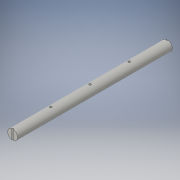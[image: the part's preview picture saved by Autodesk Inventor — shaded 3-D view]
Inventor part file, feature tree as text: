
AUTODESK INVENTOR PART (.ipt)
format: ipt  version: 2016 (Build 200138000, 138)  size: 138,752 bytes
history: native  units: in
note: dims shown in document units (in); Inventor stores cm internally (conversion verified against a paired STEP export)
features: extrude x4, sketch x3
ambient origin geometry x8: Origin, YZ Plane, XZ Plane, XY Plane, X Axis, Y Axis, Z Axis, Center Point
bodies: Solid1 (feature_tree)
feature tree (7):
  extrude  "Extrusion1"  Depth=8.0in TaperAngle=0.0deg
  extrude  "Extrusion4"  Depth=0.06in
  extrude  "Extrusion6"  Depth=2.0in TaperAngle=0.0deg
  extrude  "Extrusion7"  Depth=2.0in
  sketch  "Sketch1"  dims[d0=0.5in d1=8.0in d2=0.0in]
  sketch  "Sketch4"  dims[d13=0.06in d15=0.06in]
  sketch  "Sketch6"  dims[d16=0.1in d17=0.6in d18=0.0in d19=0.1in d20=0.06in d21=0.05in d26=0.5in d27=0.06in d28=1.0in d29=0.0in d30=2.0in d31=2.0in d33=0.25in d34=0.1in d36=0.1in d37=2.0in d38=0.1in d39=2.0in d40=1.0in d41=0.0in]
